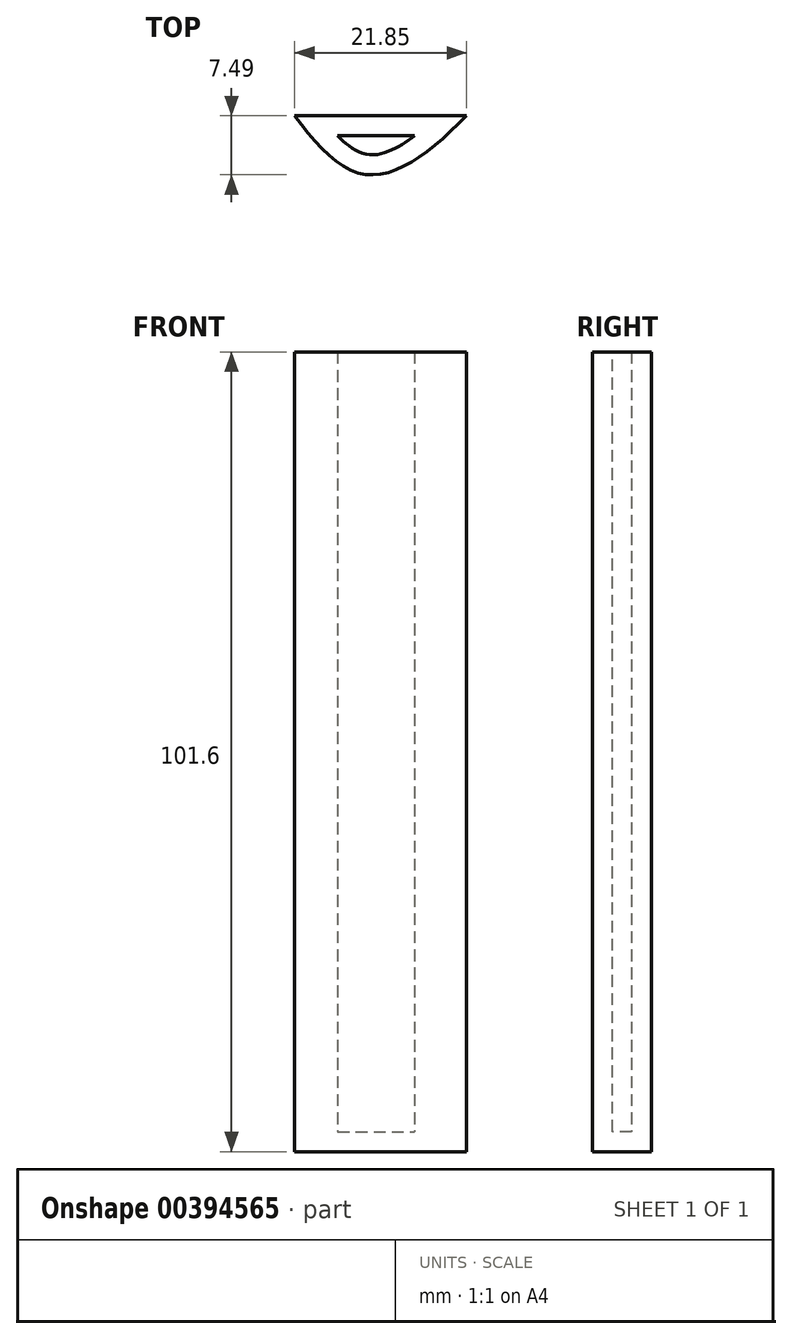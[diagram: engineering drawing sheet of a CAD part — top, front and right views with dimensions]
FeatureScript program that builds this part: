
annotation { "Feature Type Name" : "Feature", "Feature Type Description" : "" }
export const myFeature = defineFeature(function(context is Context, id is Id, definition is map)
    precondition{}
    {
        {
            var Q0;
            Q0=qCreatedBy(makeId("Top.planeOp"),FACE);
            var sketch = newSketch(context, id + "F0", { "sketchPlane" : qUnion([Q0])});
            skLineSegment(sketch, "E0.bottom", {"start": v(-7.52, 34.95) * mm, "end": v(14.33, 34.95) * mm});
            skLineSegment(sketch, "E0.top", {"start": v(-41.4, -40.3) * mm, "end": v(-17.43, -40.3) * mm});
            skLineSegment(sketch, "E0.left", {"start": v(-41.4, -26.83) * mm, "end": v(-41.4, -40.3) * mm});
            skFitSpline(sketch, "E1", {"points": [v(-27.77, 34.95) * mm, v(-16.32, 45.18) * mm, v(0, 27.89) * mm, v(21.68, 42.5) * mm, v(42.38, 53.7) * mm, v(56.5, 43.23) * mm, v(54.56, 22.04) * mm, v(32.88, 24) * mm, v(36.3, 6.45) * mm, v(67.22, -4.75) * mm, v(54.07, -36.41) * mm, v(28.98, -27.64) * mm, v(18.27, -42.99) * mm, v(-9.74, -54.68) * mm, v(-24.6, -27.4) * mm, v(-56.02, -26.91) * mm, v(-64.3, -8.16) * mm, v(-38.73, 10.35) * mm, v(-52.85, 32.03) * mm, v(-27.77, 34.95) * mm]});
            skSolve(sketch);
        }
        {
            var Q0;
            Q0=makeQuery(id+"F0.imprint","IMPRINT",FACE,{"disambiguationData":[TD([[makeQuery(id+"F0.imprint","IMPRINT",EDGE,{"derivedFrom":sQuery(id+"F0.wireOp",EDGE,"E0.bottom")}),-1.0]])]});
            extrude(context, id + "F1", {"entities" : qUnion([Q0]), "endBound" : BoundingType.SYMMETRIC, "depth" : 101.6 * mm});
        }
        {
            var Q0;
            Q0=makeQuery(id+"F1.opExtrude","CAP_FACE",FACE,{"disambiguationData":[OSD([sQuery(id+"F0.wireOp",EDGE,"E0.bottom"),sQuery(id+"F0.wireOp",EDGE,"E0.top"),sQuery(id+"F0.wireOp",EDGE,"E0.left"),sQuery(id+"F0.wireOp",EDGE,"E1"),sQuery(id+"F0.wireOp",EDGE,"E1")])],"isStart":false});
            shell(context, id + "F2", {"entities" : qUnion([Q0]), "thickness" : 2.54 * mm});
        }
    });
